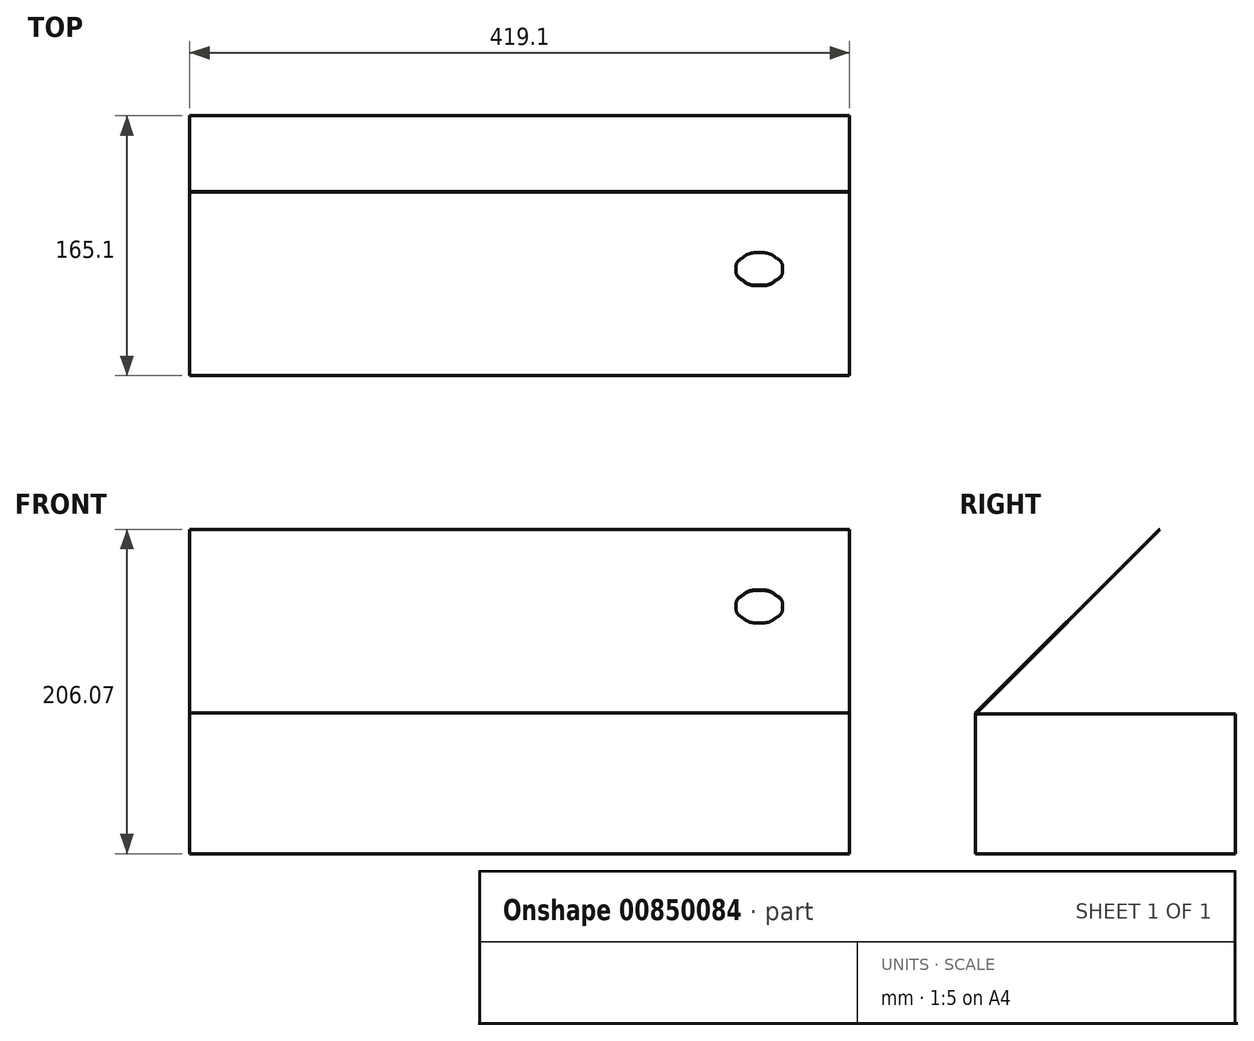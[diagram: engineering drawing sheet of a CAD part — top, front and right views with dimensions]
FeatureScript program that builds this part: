
annotation { "Feature Type Name" : "Feature", "Feature Type Description" : "" }
export const myFeature = defineFeature(function(context is Context, id is Id, definition is map)
    precondition{}
    {
        {
            var Q0;
            Q0=qCreatedBy(makeId("Right.planeOp"),FACE);
            var sketch = newSketch(context, id + "F0", { "sketchPlane" : qUnion([Q0])});
            skLineSegment(sketch, "E0.bottom", {"start": v(0, 0) * mm, "end": v(-165.1, 0) * mm});
            skLineSegment(sketch, "E0.top", {"start": v(0, 88.9) * mm, "end": v(-164.7, 88.9) * mm});
            skLineSegment(sketch, "E0.left", {"start": v(0, 0) * mm, "end": v(0, 88.9) * mm});
            skLineSegment(sketch, "E0.right", {"start": v(-165.1, 0) * mm, "end": v(-165.1, 89.32) * mm});
            skLineSegment(sketch, "E1", {"start": v(-165.1, 89.32) * mm, "end": v(-48.36, 206.07) * mm});
            skLineSegment(sketch, "E2", {"start": v(-48.36, 206.07) * mm, "end": v(-48.07, 205.78) * mm});
            skLineSegment(sketch, "E3", {"start": v(-48.07, 205.78) * mm, "end": v(-164.7, 89.15) * mm});
            skLineSegment(sketch, "E4", {"start": v(-164.7, 88.9) * mm, "end": v(-164.7, 89.15) * mm});
            skLineSegment(sketch, "E5", {"start": v(-164.7, 88.9) * mm, "end": v(-165.1, 88.9) * mm, "construction": true});
            skSolve(sketch);
        }
        {
            var Q0;
            Q0=qSketchRegion(id+"F0",true);
            extrude(context, id + "F1", {"entities" : qUnion([Q0]), "endBound" : BoundingType.SYMMETRIC, "depth" : 419.1 * mm, "offsetDistance" : 25.4 * mm});
        }
        {
            var Q0;
            Q0=makeQuery(id+"F1.opExtrude","SWEPT_FACE",FACE,{"disambiguationData":[OSD([sQuery(id+"F0.wireOp",EDGE,"E1")])]});
            var sketch = newSketch(context, id + "F2", { "sketchPlane" : qUnion([Q0])});
            skLineSegment(sketch, "E6", {"start": v(-209.83, -53.06) * mm, "end": v(-209.83, 111.25) * mm, "construction": true});
            skLineSegment(sketch, "E7", {"start": v(209.27, -53.06) * mm, "end": v(209.27, 111.25) * mm, "construction": true});
            skLineSegment(sketch, "E8", {"start": v(-209.83, -53.06) * mm, "end": v(209.27, -53.06) * mm, "construction": true});
            skLineSegment(sketch, "E9", {"start": v(-209.83, 111.25) * mm, "end": v(209.27, 111.25) * mm, "construction": true});
            skFitSpline(sketch, "E10", {"points": [v(152.12, 56.88) * mm, v(148.28, 56.88) * mm, v(144.46, 55.3) * mm, v(141.74, 52.58) * mm]});
            skFitSpline(sketch, "E11", {"points": [v(141.74, 52.58) * mm, v(139.02, 49.86) * mm, v(137.44, 46.04) * mm, v(137.44, 42.2) * mm, v(137.44, 38.35) * mm, v(139.02, 34.53) * mm, v(141.74, 31.8) * mm]});
            skFitSpline(sketch, "E12", {"points": [v(141.74, 31.8) * mm, v(144.46, 29.1) * mm, v(148.28, 27.5) * mm, v(152.12, 27.5) * mm, v(155.97, 27.5) * mm, v(159.79, 29.1) * mm, v(162.5, 31.8) * mm]});
            skFitSpline(sketch, "E13", {"points": [v(162.5, 31.8) * mm, v(165.23, 34.53) * mm, v(166.8, 38.35) * mm, v(166.8, 42.2) * mm, v(166.8, 46.04) * mm, v(165.23, 49.86) * mm, v(162.5, 52.58) * mm]});
            skFitSpline(sketch, "E14", {"points": [v(162.5, 52.58) * mm, v(159.79, 55.3) * mm, v(155.97, 56.88) * mm, v(152.12, 56.88) * mm]});
            skSolve(sketch);
        }
        {
            var Q0;
            Q0=qSketchRegion(id+"F2",true);
            var Q1;
            Q1=makeQuery(id+"F1.opExtrude","SWEPT_FACE",FACE,{"disambiguationData":[OSD([sQuery(id+"F0.wireOp",EDGE,"E3")])]});
            extrude(context, id + "F3", {"entities" : qUnion([Q0]), "operationType" : NewBodyOperationType.REMOVE, "endBound" : BoundingType.UP_TO_SURFACE, "oppositeDirection" : true, "depth" : 25.4 * mm, "endBoundEntityFace" : qUnion([Q1]), "offsetDistance" : 25.4 * mm});
        }
    });
